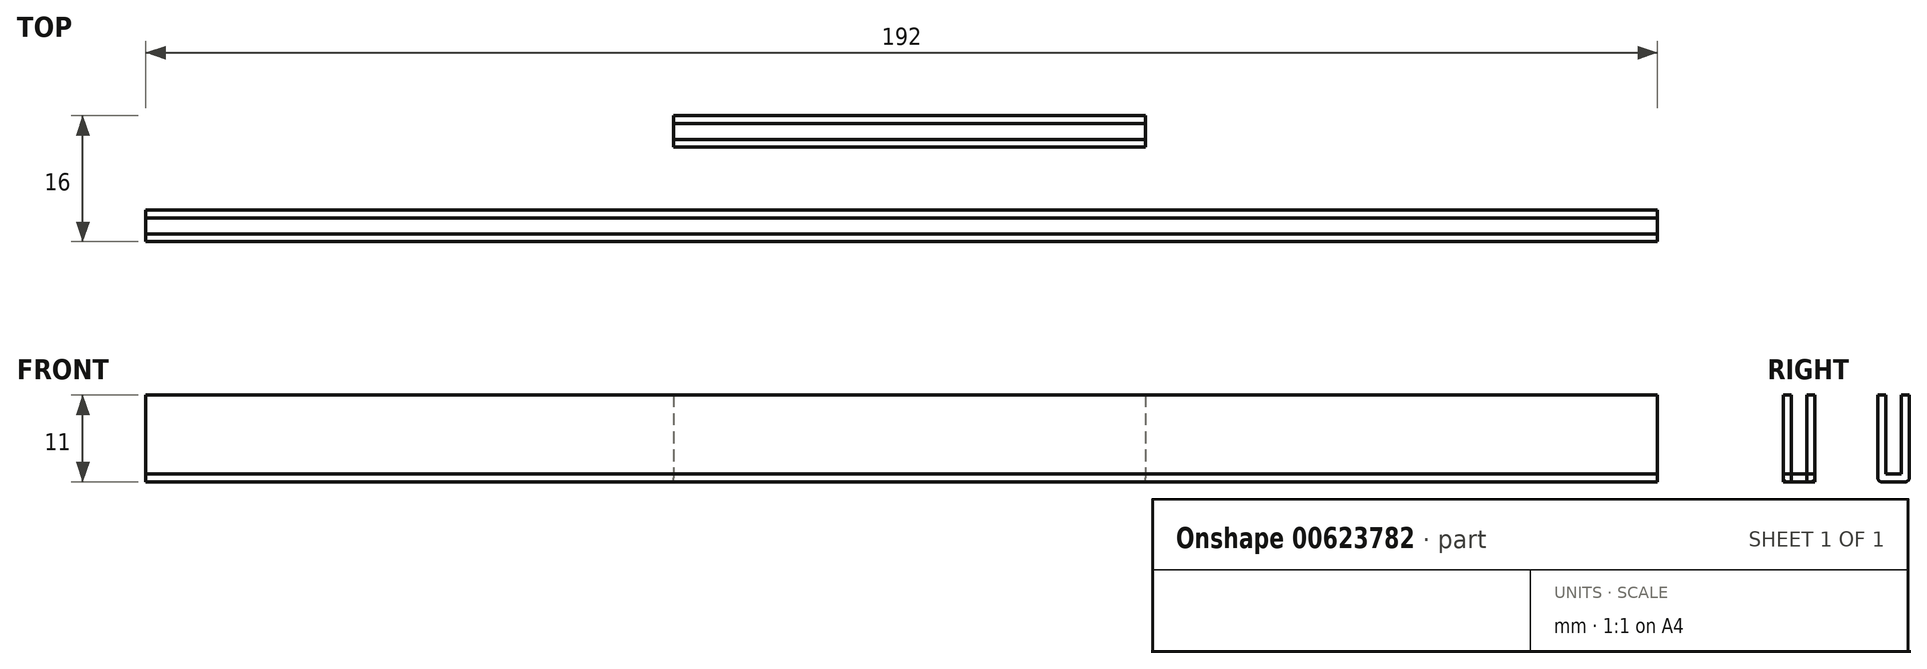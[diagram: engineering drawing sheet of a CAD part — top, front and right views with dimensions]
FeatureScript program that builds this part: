
annotation { "Feature Type Name" : "Feature", "Feature Type Description" : "" }
export const myFeature = defineFeature(function(context is Context, id is Id, definition is map)
    precondition{}
    {
        {
            var Q0;
            Q0=qCreatedBy(makeId("Top.planeOp"),FACE);
            var sketch = newSketch(context, id + "F0", { "sketchPlane" : qUnion([Q0])});
            skLineSegment(sketch, "E0.bottom", {"start": v(-30, 2) * mm, "end": v(30, 2) * mm});
            skLineSegment(sketch, "E0.top", {"start": v(-30, -2) * mm, "end": v(30, -2) * mm});
            skLineSegment(sketch, "E0.left", {"start": v(-30, 2) * mm, "end": v(-30, -2) * mm});
            skLineSegment(sketch, "E0.right", {"start": v(30, 2) * mm, "end": v(30, -2) * mm});
            skPoint(sketch, "E0.middle", {"position": v(0, 0) * mm});
            skSolve(sketch);
        }
        {
            var Q0;
            Q0=makeQuery(id+"F0.imprint","IMPRINT",FACE,{"disambiguationData":[TD([[makeQuery(id+"F0.imprint","IMPRINT",EDGE,{"derivedFrom":sQuery(id+"F0.wireOp",EDGE,"E0.bottom")}),-1.0]])]});
            extrude(context, id + "F1", {"entities" : qUnion([Q0]), "depth" : 1 * mm, "offsetDistance" : 25 * mm});
        }
        {
            var Q0;
            Q0=makeQuery(id+"F1.opExtrude","CAP_FACE",FACE,{"disambiguationData":[OSD([sQuery(id+"F0.wireOp",EDGE,"E0.bottom"),sQuery(id+"F0.wireOp",EDGE,"E0.top"),sQuery(id+"F0.wireOp",EDGE,"E0.left"),sQuery(id+"F0.wireOp",EDGE,"E0.right")])],"isStart":false});
            var sketch = newSketch(context, id + "F2", { "sketchPlane" : qUnion([Q0])});
            skLineSegment(sketch, "E1.bottom", {"start": v(-30, -2) * mm, "end": v(30, -2) * mm});
            skLineSegment(sketch, "E1.top", {"start": v(-30, -1) * mm, "end": v(30, -1) * mm});
            skLineSegment(sketch, "E1.left", {"start": v(-30, -2) * mm, "end": v(-30, -1) * mm});
            skLineSegment(sketch, "E1.right", {"start": v(30, -2) * mm, "end": v(30, -1) * mm});
            skLineSegment(sketch, "E2.bottom", {"start": v(-30, 2) * mm, "end": v(30, 2) * mm});
            skLineSegment(sketch, "E2.top", {"start": v(-30, 1) * mm, "end": v(30, 1) * mm});
            skLineSegment(sketch, "E2.left", {"start": v(-30, 2) * mm, "end": v(-30, 1) * mm});
            skLineSegment(sketch, "E2.right", {"start": v(30, 2) * mm, "end": v(30, 1) * mm});
            skSolve(sketch);
        }
        {
            var Q0;
            Q0=makeQuery(id+"F2.imprint","IMPRINT",FACE,{"disambiguationData":[TD([[makeQuery(id+"F2.imprint","IMPRINT",EDGE,{"derivedFrom":sQuery(id+"F2.wireOp",EDGE,"E2.bottom")}),-1.0]])]});
            var Q1;
            Q1=makeQuery(id+"F2.imprint","IMPRINT",FACE,{"disambiguationData":[TD([[makeQuery(id+"F2.imprint","IMPRINT",EDGE,{"derivedFrom":sQuery(id+"F2.wireOp",EDGE,"E1.bottom")}),1.0]])]});
            extrude(context, id + "F3", {"entities" : qUnion([Q0, Q1]), "operationType" : NewBodyOperationType.ADD, "depth" : 10 * mm, "offsetDistance" : 25 * mm});
        }
        {
            var Q0;
            Q0=makeQuery(id+"F1.opExtrude","CAP_EDGE",EDGE,{"disambiguationData":[OSD([sQuery(id+"F0.wireOp",EDGE,"E0.top")])],"isStart":true});
            var Q1;
            Q1=makeQuery(id+"F1.opExtrude","CAP_EDGE",EDGE,{"disambiguationData":[OSD([sQuery(id+"F0.wireOp",EDGE,"E0.bottom")])],"isStart":true});
            fillet(context, id + "F4", {"entities" : qUnion([Q0, Q1]), "radius" : .5 * mm, "tangentPropagation" : true, "allowEdgeOverflow" : false});
        }
        {
            var Q0;
            Q0=qCreatedBy(makeId("Top.planeOp"),FACE);
            var sketch = newSketch(context, id + "F5", { "sketchPlane" : qUnion([Q0])});
            skLineSegment(sketch, "E3.bottom", {"start": v(-97, -10) * mm, "end": v(95, -10) * mm});
            skLineSegment(sketch, "E3.top", {"start": v(-97, -14) * mm, "end": v(95, -14) * mm});
            skLineSegment(sketch, "E3.left", {"start": v(-97, -10) * mm, "end": v(-97, -14) * mm});
            skLineSegment(sketch, "E3.right", {"start": v(95, -10) * mm, "end": v(95, -14) * mm});
            skLineSegment(sketch, "E4", {"start": v(0, 0) * mm, "end": v(0, -10) * mm, "construction": true});
            skLineSegment(sketch, "E5", {"start": v(0, -10) * mm, "end": v(95, -10) * mm, "construction": true});
            skLineSegment(sketch, "E6.left", {"start": v(-97, -10) * mm, "end": v(-97, -10) * mm});
            skLineSegment(sketch, "E6.right", {"start": v(95, -10) * mm, "end": v(95, -10) * mm});
            skLineSegment(sketch, "E7.top", {"start": v(-97, -11) * mm, "end": v(95, -11) * mm});
            skLineSegment(sketch, "E7.left", {"start": v(-97, -10) * mm, "end": v(-97, -11) * mm});
            skLineSegment(sketch, "E7.right", {"start": v(95, -10) * mm, "end": v(95, -11) * mm});
            skLineSegment(sketch, "E8.top", {"start": v(-97, -13) * mm, "end": v(95, -13) * mm});
            skLineSegment(sketch, "E8.left", {"start": v(-97, -14) * mm, "end": v(-97, -13) * mm});
            skLineSegment(sketch, "E8.right", {"start": v(95, -14) * mm, "end": v(95, -13) * mm});
            skSolve(sketch);
        }
        {
            var Q0;
            Q0=makeQuery(id+"F5.imprint","IMPRINT",FACE,{"disambiguationData":[TD([[makeQuery(id+"F5.imprint","IMPRINT",EDGE,{"derivedFrom":sQuery(id+"F5.wireOp",EDGE,"E3.bottom")}),-1.0]])]});
            var Q1;
            Q1=makeQuery(id+"F5.imprint","IMPRINT",FACE,{"disambiguationData":[TD([[makeQuery(id+"F5.imprint","IMPRINT",EDGE,{"derivedFrom":sQuery(id+"F5.wireOp",EDGE,"E3.top")}),1.0]])]});
            extrude(context, id + "F6", {"entities" : qUnion([Q0, Q1]), "depth" : 11 * mm, "offsetDistance" : 25 * mm});
        }
        {
            var Q0;
            Q0=makeQuery(id+"F5.imprint","IMPRINT",FACE,{"disambiguationData":[TD([[makeQuery(id+"F5.imprint","IMPRINT",EDGE,{"derivedFrom":sQuery(id+"F5.wireOp",EDGE,"E3.left")}),1.0]])]});
            extrude(context, id + "F7", {"entities" : qUnion([Q0]), "depth" : 1 * mm, "offsetDistance" : 25 * mm});
        }
        {
            var Q0;
            Q0=makeQuery(id+"F6.opExtrude","CAP_EDGE",EDGE,{"disambiguationData":[OSD([sQuery(id+"F5.wireOp",EDGE,"E3.top")])],"isStart":true});
            var Q1;
            Q1=makeQuery(id+"F6.opExtrude","CAP_EDGE",EDGE,{"disambiguationData":[OSD([sQuery(id+"F5.wireOp",EDGE,"E3.bottom")])],"isStart":true});
            fillet(context, id + "F8", {"entities" : qUnion([Q0, Q1]), "radius" : .5 * mm, "tangentPropagation" : true, "allowEdgeOverflow" : false});
        }
    });
